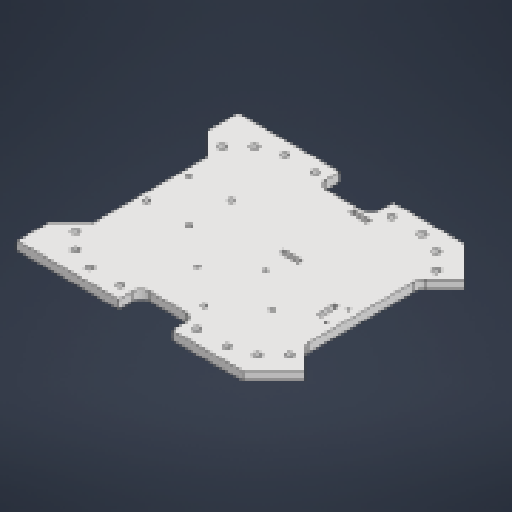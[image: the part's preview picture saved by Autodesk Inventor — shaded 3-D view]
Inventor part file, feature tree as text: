
AUTODESK INVENTOR PART (.ipt)
format: ipt  version: 2023 (Build 270158000, 158)  size: 338,944 bytes
history: native  units: in
note: dims shown in document units (in); Inventor stores cm internally (conversion verified against a paired STEP export)
features: sketch x8, extrude x5, hole x5, other x3, fillet x1, reference x1
ambient origin geometry x8: Origin, YZ Plane, XZ Plane, XY Plane, X Axis, Y Axis, Z Axis, Center Point
bodies: Body1 (feature_tree)
feature tree (23):
  extrude  "Extrusion8"  Depth=5.0in
  hole  "Hole3"  [1 undecoded]
  hole  "Hole5"  [1 undecoded]
  extrude  "Extrusion14"  Depth=1.2008in
  sketch  "Sketch18"  dims[d90=0.249in]
  extrude  "Extrusion16"  Depth=0.25in
  sketch  "Sketch23"  dims[d110=1.2008in d111=1.2008in]
  extrude  "Extrusion18"  Depth=0.25in
  extrude  "Extrusion19"  Depth=0.25in
  hole  "Hole9"  [1 undecoded]
  fillet  "Fillet5"  Radius=0.125in
  hole  "Hole10"  [1 undecoded]
  hole  "Hole11"  [1 undecoded]
  sketch  "Sketch14"  dims[d0=6.0in d1=5.0in]
  sketch  "Sketch17"  dims[d31=0.25in d32=0.0in d89=0.3125in]
  reference  "Reference38"
  sketch  "Sketch19"  dims[d91=0.063in d92=0.75in d93=0.375in d94=0.25in d95=0.5635in d96=1.0in d97=0.8108in d109=1.2008in]
  sketch  "Sketch24"  dims[d112=1.2008in]
  sketch  "Sketch25"  dims[d113=0.1575in d114=0.75in d115=0.375in d116=0.25in d117=0.5635in d118=1.0in d119=0.8108in d120=0.25in]
  sketch  "Sketch26"  dims[d121=0.125in d122=0.25in d123=0.25in d124=0.125in d125=0.25in d126=0.4375in d127=0.0in d130=0.125in d131=0.5in d132=0.0625in d133=1.0in d134=0.0in d167=1.25in d169=0.9in d170=2.0in d172=1.7064in d173=1.6899in d174=0.25in d175=0.0in d176=0.25in d177=0.0in d178=0.195in d179=0.75in d180=0.375in d181=0.25in d182=0.5635in d183=0.41in d184=0.0in d185=0.8599in d186=0.375in d187=0.375in d189=0.25in d190=0.33in d191=0.063in d192=0.75in d193=0.375in d194=0.25in d195=0.5635in d196=0.41in d197=0.0in d198=0.063in d199=0.75in d200=0.375in d201=0.25in d202=0.5635in d203=0.41in d204=0.0in d81=0.5in d82=0.0344in d83=0.5in d84=0.0344in]
  other  "<userpath>\Documents\GitHub\SDP-Kepler-1708b\Assembly.iam"
  other  "Assembly.iam"
  other  "LiPo:1"
note: 5 required parameter values undecoded (feature->parameter linkage not recoverable at this tier; creation-order binding heuristic only, values carry confidence <= 0.55)
